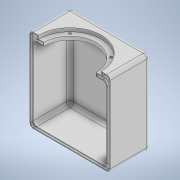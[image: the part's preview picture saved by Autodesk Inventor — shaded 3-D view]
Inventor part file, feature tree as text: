
AUTODESK INVENTOR PART (.ipt)
format: ipt  version: 2022 (Build 260153000, 153)  size: 289,792 bytes
history: native  units: in
note: dims shown in document units (in); Inventor stores cm internally (conversion verified against a paired STEP export)
features: extrude x9, sketch x9, fillet x2, projected_geometry x2, plane x1, split x1
ambient origin geometry x8: Origin, YZ Plane, XZ Plane, XY Plane, X Axis, Y Axis, Z Axis, Center Point
bodies: Solid1 (feature_tree)
feature tree (24):
  extrude  "Extrusion1"  Depth=4.1339in
  extrude  "Extrusion2"  Depth=2.0669in
  extrude  "Extrusion3"  Depth=0.1969in TaperAngle=0.0deg
  extrude  "Extrusion4"  Depth=0.1969in TaperAngle=0.0deg
  extrude  "Extrusion5"  Depth=0.1969in TaperAngle=0.0deg
  extrude  "Extrusion6"  Depth=0.1969in TaperAngle=0.0deg
  extrude  "Extrusion7"  Depth=0.1969in TaperAngle=0.0deg
  extrude  "Extrusion8"  Depth=3.2874in
  plane  "Work Plane1"
  fillet  "Fillet2"  Radius=0.1417in
  fillet  "Fillet3"  Radius=0.1417in
  sketch  "Sketch13"  dims[d25=0.1417in d26=45.0deg d27=0.1969in d28=0.0in d30=0.1969in d31=0.1969in d32=0.0394in d35=0.1181in d36=0.0in d33=0.0197in d34=0.0344in]
  split  "Split2"
  extrude  "Extrusion10"  TaperAngle=45.0deg  [1 undecoded]
  sketch  "Sketch1"  dims[d0=4.1339in d1=4.1339in]
  sketch  "Sketch3"  dims[d2=2.0669in d3=2.0669in]
  sketch  "Sketch4"  dims[d4=2.9528in d5=0.1969in d6=0.0in]
  sketch  "Sketch6"  dims[d7=4.1339in d8=0.1969in d9=0.0in]
  sketch  "Sketch7"  dims[d10=0.1969in d11=0.0in d12=0.1969in d13=0.0in]
  sketch  "Sketch8"  dims[d14=0.1969in d15=0.0in d16=0.1969in d17=0.0in]
  sketch  "Sketch9"  dims[d18=3.5433in d19=0.1969in d20=0.0in]
  projected_geometry  "Projected Loop1"
  sketch  "Sketch10"  dims[d21=0.1417in d22=3.2874in d23=0.1417in d24=0.1417in]
  projected_geometry  "Project Cut Edges2"
note: 1 required parameter value undecoded (feature->parameter linkage not recoverable at this tier; creation-order binding heuristic only, values carry confidence <= 0.55)
